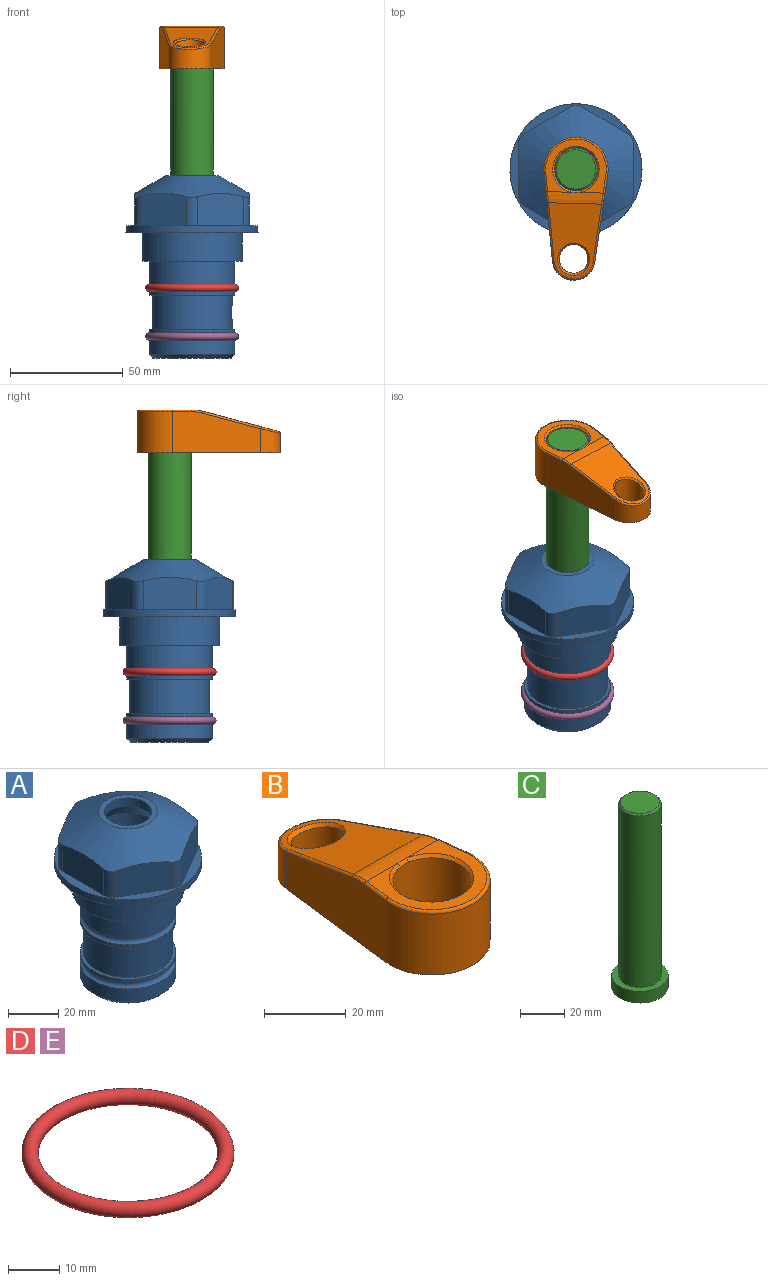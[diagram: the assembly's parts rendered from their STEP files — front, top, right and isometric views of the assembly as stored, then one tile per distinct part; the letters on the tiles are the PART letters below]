
ASSEMBLY  parts=5 mates=4
PART A: 36 faces, bbox 58.7x58.7x81 mm
  f0: cylinder r=17.78mm len=35.56mm, axis (0,0,1), area 1670.8mm2, adj f23,f24,f31
  f1: cylinder r=19.05mm len=38.1mm, axis (0,0,1), area 1191.9mm2, adj f26,f27,f30
  f2: plane 58.66x58.66mm, normal (0,0,-1), area 1150.6mm2, adj f3,f28
  f3: cylinder r=29.33mm len=58.66mm, axis (0,0,-1), area 585.1mm2, adj f2,f4
  f4: plane 58.66x58.66mm, normal (0,0,1), area 475.9mm2, adj f3,f5,f6,f7,f8,f9,f10,f11
  f5: plane 20.32x14.34mm, normal (-0.5,0.87,0), area 324.4mm2, adj f4,f15,f16,f17
  f6: plane 20.32x14.34mm, normal (0.5,0.87,0), area 324.4mm2, adj f4,f14,f15,f17
  f7: plane 23.48x14.34mm, normal (1,0,0), area 324.4mm2, adj f4,f13,f14,f17
  f8: plane 20.32x14.34mm, normal (0.5,-0.87,0), area 324.4mm2, adj f4,f12,f13,f17
  f9: plane 20.32x14.34mm, normal (-0.5,-0.87,0), area 324.4mm2, adj f4,f11,f12,f17
  f10: plane 23.48x14.34mm, normal (-1,0,0), area 324.4mm2, adj f4,f11,f16,f17
  f11: cylinder r=5.08mm len=12.85mm, axis (0,0,-1), area 67.2mm2, adj f4,f9,f10,f17
  f12: cylinder r=5.08mm len=12.85mm, axis (0,0,-1), area 67.2mm2, adj f4,f8,f9,f17
  f13: cylinder r=5.08mm len=12.85mm, axis (0,0,-1), area 67.2mm2, adj f4,f7,f8,f17
  f14: cylinder r=5.08mm len=12.85mm, axis (0,0,-1), area 67.2mm2, adj f4,f6,f7,f17
  f15: cylinder r=5.08mm len=12.85mm, axis (0,0,-1), area 67.2mm2, adj f4,f5,f6,f17
  f16: cylinder r=5.08mm len=12.85mm, axis (0,0,-1), area 67.2mm2, adj f4,f5,f10,f17
  f17: cone r=11.73mm half-angle=60deg, axis (0,0,-1), area 2071.8mm2, adj f5,f6,f7,f8,f9,f10,f11,f12
  f18: plane 23.46x23.46mm, normal (0,0,1), area 147.4mm2, adj f17,f35
  f19: plane 34.93x34.93mm, normal (0,0,-1), area 958mm2, adj f29
  f20: cylinder r=19.05mm len=38.1mm, axis (0,0,1), area 760.1mm2, adj f21,f29
  f21: torus R=19.05mm, axis (0,0,1), area 565.3mm2, adj f20,f22
  f22: cylinder r=19.05mm len=38.1mm, axis (0,0,1), area 190mm2, adj f21,f23
  f23: plane 38.1x38.1mm, normal (0,0,1), area 146.9mm2, adj f0,f22
  f24: plane 38.1x38.1mm, normal (0,0,-1), area 146.9mm2, adj f0,f25
  f25: cylinder r=19.05mm len=38.1mm, axis (0,0,1), area 190mm2, adj f24,f26
  f26: torus R=19.05mm, axis (0,0,1), area 565.3mm2, adj f1,f25
  f27: plane 44.45x44.45mm, normal (0,0,-1), area 411.7mm2, adj f1,f28
  f28: cylinder r=22.23mm len=44.45mm, axis (0,0,1), area 1773.5mm2, adj f2,f27
  f29: cone r=19.05mm half-angle=45deg, axis (0,0,1), area 257.5mm2, adj f19,f20
  f30: cylinder r=3.17mm len=6.75mm, axis (-1,0,0), area 128mm2, adj f1,f33
  f31: cylinder r=3.17mm len=6.35mm, axis (-1,0,0), area 102.5mm2, adj f0,f33
  f32: plane 25.4x25.4mm, normal (0,0,1), area 506.7mm2, adj f33
  f33: cylinder r=12.7mm len=66.42mm, axis (0,0,-1), area 5236.2mm2, adj f30,f31,f32,f34
  f34: cone r=9.53mm half-angle=30deg, axis (0,0,-1), area 443.4mm2, adj f33,f35
  f35: cylinder r=9.53mm len=19.05mm, axis (0,0,-1), area 240.9mm2, adj f18,f34
PART B: 31 faces, bbox 31.7x65.5x19.8 mm
  f0: plane 39.12x18.26mm, normal (0.99,0.12,0), area 612.2mm2, adj f1,f4,f7,f11,f13,f15
  f1: cylinder r=9.53mm len=18.91mm, axis (0,0,-1), area 296.1mm2, adj f0,f2,f7,f17
  f2: plane 39.12x18.26mm, normal (-0.99,0.12,0), area 612.2mm2, adj f1,f4,f7,f12,f14,f16
  f3: cylinder r=6.35mm len=12.7mm, axis (0,0,-1), area 362.4mm2, adj f7,f18
  f4: cylinder r=14.29mm len=28.58mm, axis (0,0,-1), area 882.2mm2, adj f0,f2,f7,f10
  f5: cylinder r=9.53mm len=19.05mm, axis (0,0,-1), area 1092.6mm2, adj f7,f19,f20
  f6: plane 26.99x23.69mm, normal (0,0,1), area 216.2mm2, adj f9,f10,f11,f12,f19
  f7: plane 63.5x28.58mm, normal (0,0,-1), area 661.8mm2, adj f0,f1,f2,f3,f4,f5,f22,f23
  f8: plane 33.52x23.6mm, normal (0,0.26,0.97), area 486mm2, adj f9,f15,f16,f17,f18
  f9: cylinder r=19.05mm len=24.72mm, axis (1,0,0), area 120.4mm2, adj f6,f8,f13,f14,f20
  f10: torus R=13.49mm, axis (0,0,1), area 59mm2, adj f4,f6,f11,f12
  f11: cylinder r=0.79mm len=8.67mm, axis (0.12,-0.99,0), area 10.8mm2, adj f0,f6,f10,f13
  f12: cylinder r=0.79mm len=8.67mm, axis (0.12,0.99,0), area 10.8mm2, adj f2,f6,f10,f14
  f13: bspline ~4.95x1.42mm, area 6.1mm2, adj f0,f9,f11,f15
  f14: bspline ~4.95x1.42mm, area 6.1mm2, adj f2,f9,f12,f16
  f15: cylinder r=0.79mm len=25.95mm, axis (0.12,-0.96,0.26), area 32.9mm2, adj f0,f8,f13,f17
  f16: cylinder r=0.79mm len=25.95mm, axis (0.12,0.96,-0.26), area 32.9mm2, adj f2,f8,f14,f17
  f17: bspline ~18.91x8.38mm, area 30mm2, adj f1,f8,f15,f16
  f18: bspline ~14.29x14.29mm, area 48.3mm2, adj f3,f8
  f19: cone r=9.53mm half-angle=45deg, axis (0,0,1), area 66.5mm2, adj f5,f6,f20
  f20: bspline ~3.22x0.96mm, area 3.5mm2, adj f5,f9,f19
  f21: plane 2.75x2.72mm, normal (0,0,-1), area 2.9mm2, adj f23,f25,f28
  f22: plane 23.05x15.88mm, normal (-0.99,-0.12,0), area 323.6mm2, adj f7,f25,f26,f27,f28,f29
  f23: plane 23.05x15.88mm, normal (0.99,-0.12,0), area 323.6mm2, adj f7,f21,f25,f27,f28,f30
  f24: cylinder r=9.53mm len=10.69mm, axis (0,0,-1), area 114.7mm2, adj f7,f27,f29,f30
  f25: cylinder r=12.7mm len=20.59mm, axis (0,0,-1), area 381.1mm2, adj f7,f21,f22,f23,f26,f28
  f26: plane 2.75x2.72mm, normal (0,0,-1), area 2.9mm2, adj f22,f25,f28
  f27: plane 19.72x18.37mm, normal (0,-0.26,-0.97), area 291.8mm2, adj f22,f23,f24,f28,f29,f30
  f28: cylinder r=15.88mm len=19.92mm, axis (1,0,0), area 54.8mm2, adj f21,f22,f23,f25,f26,f27
  f29: cylinder r=1.59mm len=11mm, axis (0,0,-1), area 34.7mm2, adj f7,f22,f24,f27
  f30: cylinder r=1.59mm len=11mm, axis (0,0,-1), area 34.7mm2, adj f7,f23,f24,f27
PART C: 6 faces, bbox 25.4x25.4x101.6 mm
  f0: plane 17.46x17.46mm, normal (0,0,1), area 239.5mm2, adj f5
  f1: plane 25.4x25.4mm, normal (0,0,-1), area 506.7mm2, adj f2
  f2: cylinder r=12.7mm len=25.4mm, axis (0,0,1), area 506.7mm2, adj f1,f3
  f3: plane 25.4x25.4mm, normal (0,0,1), area 221.7mm2, adj f2,f4
  f4: cylinder r=9.53mm len=94.46mm, axis (0,0,1), area 5653mm2, adj f3,f5
  f5: cone r=8.73mm half-angle=45deg, axis (0,0,-1), area 64.4mm2, adj f0,f4
PART D: 1 faces, bbox 44.7x44.7x3.2 mm
  f0: torus R=19.05mm, axis (0,0,1), area 1193.9mm2
PART E: same geometry as D
PLACE A at identity fixed
PLACE B rot(axis=(0,0,1),178.5deg) t=(0,0,28.35)mm
PLACE C rot(axis=(0,0,1),178.5deg) t=(0,0,27.55)mm
PLACE D at identity
PLACE E rot(axis=(0.07,1,-0.05),0deg) t=(0,0,-21.59)mm
MATE fastened B.f4 <-> C.f2  axis (0,0,-1) through (0,0,91.05)mm
MATE fastened A.f0 <-> E.f0  axis (0,0,1) through (0,0,-46.1)mm
MATE cylindrical A.f0 <-> C.f2  axis (0,0,1) through (0,0,-50.55)mm
MATE fastened A.f0 <-> D.f0  axis (0,0,1) through (0,0,-24.51)mm
